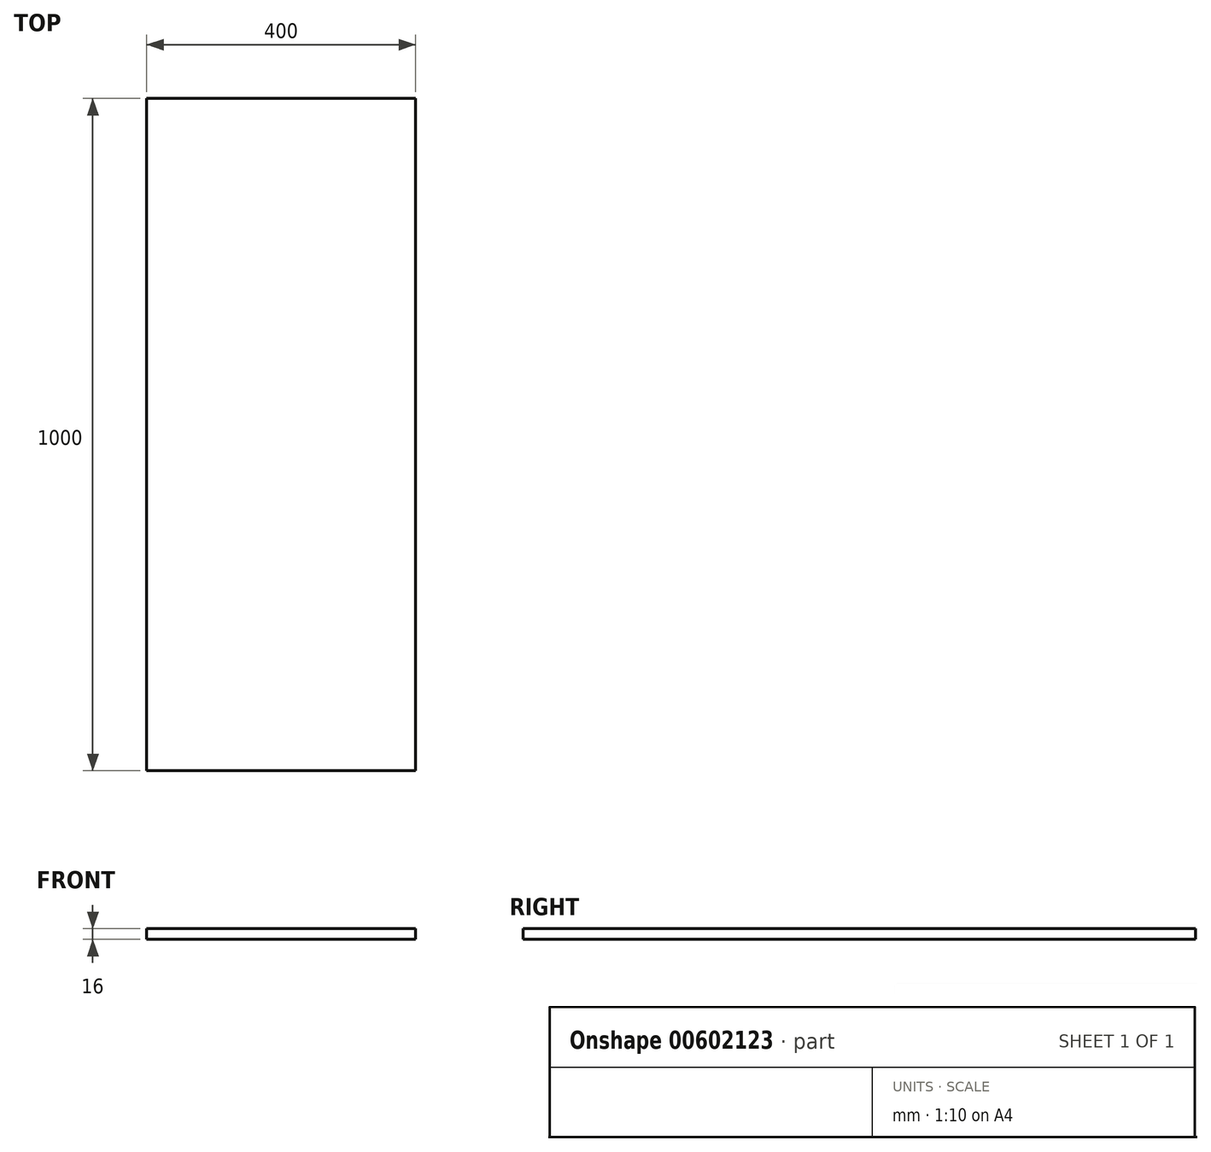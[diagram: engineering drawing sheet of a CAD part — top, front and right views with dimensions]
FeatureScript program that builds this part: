
annotation { "Feature Type Name" : "Feature", "Feature Type Description" : "" }
export const myFeature = defineFeature(function(context is Context, id is Id, definition is map)
    precondition{}
    {
        {
            var Q0;
            Q0=qCreatedBy(makeId("Top.planeOp"),FACE);
            var sketch = newSketch(context, id + "F0", { "sketchPlane" : qUnion([Q0])});
            skLineSegment(sketch, "E0.bottom", {"start": v(0, 0) * mm, "end": v(400, 0) * mm});
            skLineSegment(sketch, "E0.top", {"start": v(0, -1000) * mm, "end": v(400, -1000) * mm});
            skLineSegment(sketch, "E0.left", {"start": v(0, 0) * mm, "end": v(0, -1000) * mm});
            skLineSegment(sketch, "E0.right", {"start": v(400, 0) * mm, "end": v(400, -1000) * mm});
            skSolve(sketch);
        }
        {
            var Q0;
            Q0 = qSketchRegion(id + "F0", true);
            extrude(context, id + "F1", {"entities" : qUnion([Q0]), "depth" : 16 * mm, "offsetDistance" : 25 * mm});
        }
    });
